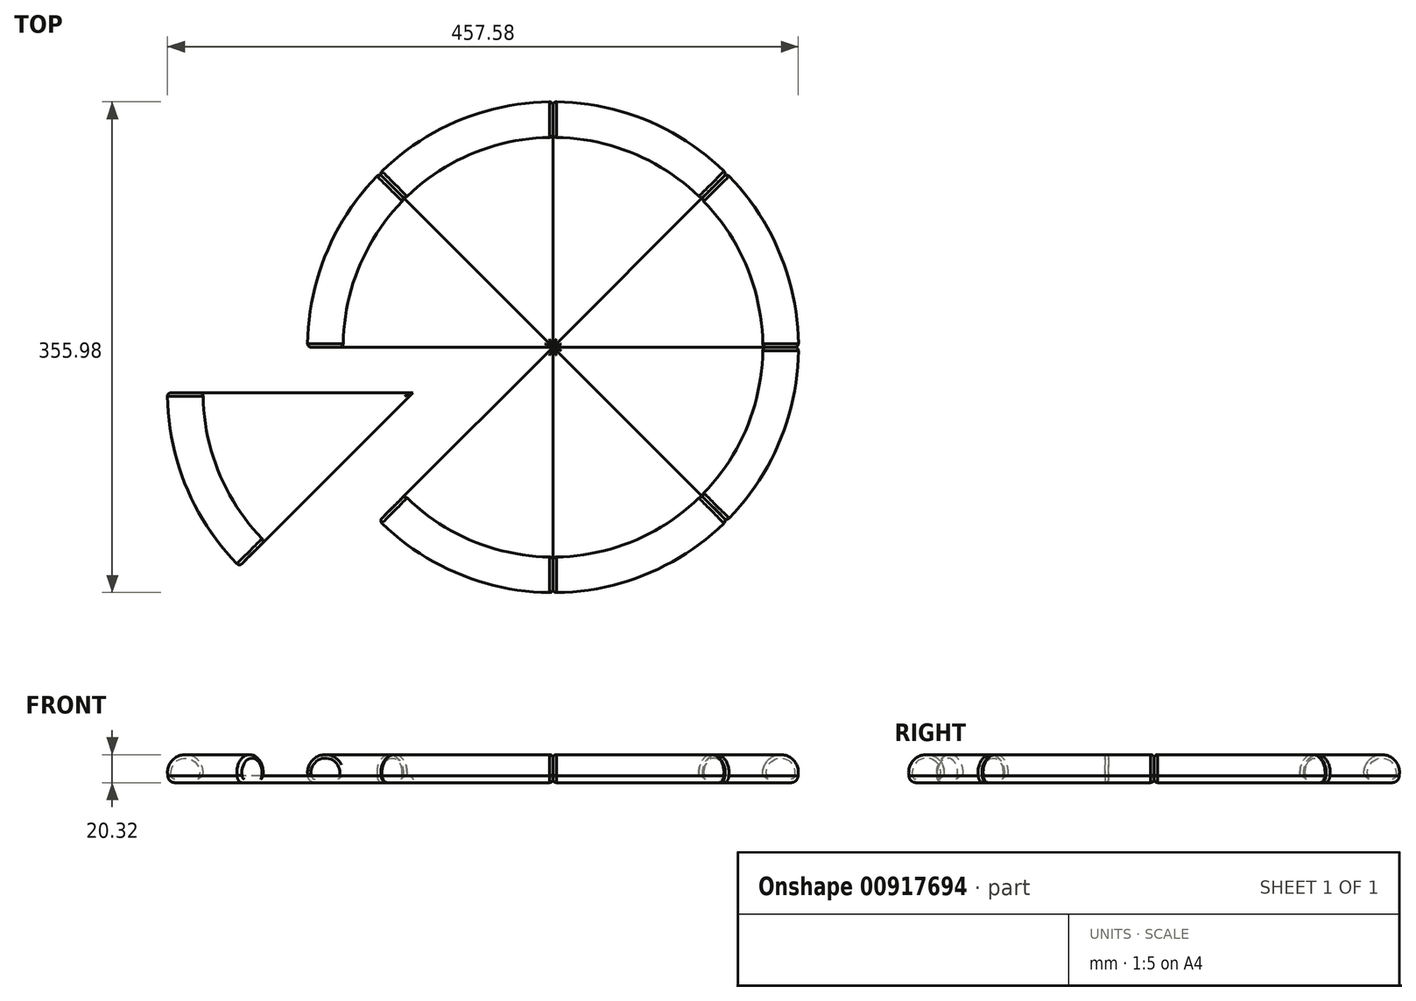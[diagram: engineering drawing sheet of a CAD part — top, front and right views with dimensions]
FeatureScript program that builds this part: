
annotation { "Feature Type Name" : "Feature", "Feature Type Description" : "" }
export const myFeature = defineFeature(function(context is Context, id is Id, definition is map)
    precondition{}
    {
        {
            var Q0;
            Q0=qCreatedBy(makeId("Top.planeOp"),FACE);
            var sketch = newSketch(context, id + "F0", { "sketchPlane" : qUnion([Q0])});
            skCircle(sketch, "E0", {"center": v(0, 0) * mm, "radius": 177.8 * mm});
            skSolve(sketch);
        }
        {
            var Q0;
            Q0=qCreatedBy(makeId("Front.planeOp"),FACE);
            var sketch = newSketch(context, id + "F1", { "sketchPlane" : qUnion([Q0])});
            skLineSegment(sketch, "E1.0", {"start": v(-177.8, 0) * mm, "end": v(177.8, 0) * mm});
            skArc(sketch, "E2", {"start": v(-152.4, 0) * mm, "mid": v(-165.1, 15.24) * mm, "end": v(-177.8, 0) * mm});
            skSolve(sketch);
        }
        {
            var Q0;
            {var subQ0=sQuery(id+"F1.wireOp",EDGE,"E2");Q0=makeQuery(id+"F1.imprint","IMPRINT",FACE,{"disambiguationData":[TD([[makeQuery(id+"F1.imprint","IMPRINT",EDGE,{"derivedFrom":subQ0}),1.0]])]});}
            var Q1;
            Q1=sQuery(id+"F0.wireOp",EDGE,"E0");
            revolve(context, id + "F2", {"surfaceOperationType" : NewSurfaceOperationType.NEW, "entities" : qUnion([Q0]), "axis" : qUnion([Q1]), "revolveType" : RevolveType.FULL});
        }
        {
            var Q0;
            Q0 = qSketchRegion(id + "F0", true);
            extrude(context, id + "F3", {"entities" : qUnion([Q0]), "operationType" : NewBodyOperationType.ADD, "oppositeDirection" : true, "depth" : 5.08 * mm, "offsetDistance" : 25.4 * mm});
        }
        {
            var Q0;
            Q0=makeQuery(id+"F3.opExtrude","CAP_EDGE",EDGE,{"disambiguationData":[OSD([sQuery(id+"F0.wireOp",EDGE,"E0")])],"isStart":false});
            fillet(context, id + "F4", {"entities" : qUnion([Q0]), "radius" : 5.08 * mm, "tangentPropagation" : true, "allowEdgeOverflow" : false});
        }
        {
            var Q0;
            Q0=qCreatedBy(makeId("Front.planeOp"),FACE);
            var sketch = newSketch(context, id + "F5", { "sketchPlane" : qUnion([Q0])});
            skLineSegment(sketch, "E3.right", {"start": v(-196.44, -103.09) * mm, "end": v(-196.44, 103.09) * mm});
            skPoint(sketch, "E3.middle", {"position": v(0, 0) * mm});
            skLineSegment(sketch, "E4", {"start": v(0, 0) * mm, "end": v(0, 103.09) * mm});
            skLineSegment(sketch, "E5", {"start": v(0, 0) * mm, "end": v(0, -103.09) * mm});
            skLineSegment(sketch, "E6", {"start": v(0, 103.09) * mm, "end": v(-196.44, 103.09) * mm});
            skLineSegment(sketch, "E7", {"start": v(0, -103.09) * mm, "end": v(-196.44, -103.09) * mm});
            skPoint(sketch, "E3.left.end.orphan", {"position": v(196.44, 103.09) * mm});
            skPoint(sketch, "E3.bottom.start.orphan", {"position": v(196.44, -103.09) * mm});
            skSolve(sketch);
        }
        {
            var Q0;
            Q0=makeQuery(id+"F5.imprint","IMPRINT",FACE,{"disambiguationData":[TD([[makeQuery(id+"F5.imprint","IMPRINT",EDGE,{"derivedFrom":sQuery(id+"F5.wireOp",EDGE,"E3.right")}),-1.0]])]});
            var Q1;
            Q1=sQuery(id+"F5.wireOp",EDGE,"E4");
            revolve(context, id + "F6", {"operationType" : NewBodyOperationType.REMOVE, "surfaceOperationType" : NewSurfaceOperationType.NEW, "entities" : qUnion([Q0]), "axis" : qUnion([Q1]), "revolveType" : RevolveType.ONE_DIRECTION, "oppositeDirection" : true, "angle" : 315 * degree});
        }
        {
            var Q0;
            Q0=makeQuery(id+"F6.boolean.opBoolean","INTERSECT",EDGE,{"derivedFrom":[makeQuery(id+"F3.opExtrude","CAP_FACE",FACE,{"disambiguationData":[OSD([sQuery(id+"F0.wireOp",EDGE,"E0")])],"isStart":true}),makeQuery(id+"F6.opRevolve","CAP_FACE",FACE,{"disambiguationData":[OSD([sQuery(id+"F5.wireOp",EDGE,"E3.right"),sQuery(id+"F5.wireOp",EDGE,"E4"),sQuery(id+"F5.wireOp",EDGE,"E5"),sQuery(id+"F5.wireOp",EDGE,"E6"),sQuery(id+"F5.wireOp",EDGE,"E7")])],"isStart":false})]});
            var Q1;
            Q1=makeQuery(id+"F6.boolean.opBoolean","INTERSECT",EDGE,{"derivedFrom":[makeQuery(id+"F3.opExtrude","CAP_FACE",FACE,{"disambiguationData":[OSD([sQuery(id+"F0.wireOp",EDGE,"E0")])],"isStart":true}),makeQuery(id+"F6.opRevolve","CAP_FACE",FACE,{"disambiguationData":[OSD([sQuery(id+"F5.wireOp",EDGE,"E3.right"),sQuery(id+"F5.wireOp",EDGE,"E4"),sQuery(id+"F5.wireOp",EDGE,"E5"),sQuery(id+"F5.wireOp",EDGE,"E6"),sQuery(id+"F5.wireOp",EDGE,"E7")])],"isStart":true})]});
            var Q2;
            Q2=makeQuery(id+"F6.boolean.opBoolean","INTERSECT",EDGE,{"derivedFrom":[makeQuery(id+"F2.opRevolve","SWEPT_FACE",FACE,{"disambiguationData":[OSD([sQuery(id+"F1.wireOp",EDGE,"E2")])]}),makeQuery(id+"F6.opRevolve","CAP_FACE",FACE,{"disambiguationData":[OSD([sQuery(id+"F5.wireOp",EDGE,"E3.right"),sQuery(id+"F5.wireOp",EDGE,"E4"),sQuery(id+"F5.wireOp",EDGE,"E5"),sQuery(id+"F5.wireOp",EDGE,"E6"),sQuery(id+"F5.wireOp",EDGE,"E7")])],"isStart":true})]});
            var Q3;
            Q3=makeQuery(id+"F6.boolean.opBoolean","INTERSECT",EDGE,{"derivedFrom":[makeQuery(id+"F4.opFillet","BLEND_FACE",FACE,{"disambiguationData":[OSD([sQuery(id+"F0.wireOp",EDGE,"E0")])]}),makeQuery(id+"F6.opRevolve","CAP_FACE",FACE,{"disambiguationData":[OSD([sQuery(id+"F5.wireOp",EDGE,"E3.right"),sQuery(id+"F5.wireOp",EDGE,"E4"),sQuery(id+"F5.wireOp",EDGE,"E5"),sQuery(id+"F5.wireOp",EDGE,"E6"),sQuery(id+"F5.wireOp",EDGE,"E7")])],"isStart":true})]});
            var Q4;
            Q4=makeQuery(id+"F6.boolean.opBoolean","INTERSECT",EDGE,{"derivedFrom":[makeQuery(id+"F2.opRevolve","SWEPT_FACE",FACE,{"disambiguationData":[OSD([sQuery(id+"F1.wireOp",EDGE,"E2")])]}),makeQuery(id+"F6.opRevolve","CAP_FACE",FACE,{"disambiguationData":[OSD([sQuery(id+"F5.wireOp",EDGE,"E3.right"),sQuery(id+"F5.wireOp",EDGE,"E4"),sQuery(id+"F5.wireOp",EDGE,"E5"),sQuery(id+"F5.wireOp",EDGE,"E6"),sQuery(id+"F5.wireOp",EDGE,"E7")])],"isStart":false})]});
            var Q5;
            Q5=makeQuery(id+"F6.boolean.opBoolean","INTERSECT",EDGE,{"derivedFrom":[makeQuery(id+"F4.opFillet","BLEND_FACE",FACE,{"disambiguationData":[OSD([sQuery(id+"F0.wireOp",EDGE,"E0")])]}),makeQuery(id+"F6.opRevolve","CAP_FACE",FACE,{"disambiguationData":[OSD([sQuery(id+"F5.wireOp",EDGE,"E3.right"),sQuery(id+"F5.wireOp",EDGE,"E4"),sQuery(id+"F5.wireOp",EDGE,"E5"),sQuery(id+"F5.wireOp",EDGE,"E6"),sQuery(id+"F5.wireOp",EDGE,"E7")])],"isStart":false})]});
            fillet(context, id + "F7", {"entities" : qUnion([Q0, Q1, Q2, Q3, Q4, Q5]), "radius" : 2.54 * mm, "tangentPropagation" : true, "allowEdgeOverflow" : false});
        }
        {
            var Q0;
            Q0=qCreatedBy(makeId("Front.planeOp"),FACE);
            var sketch = newSketch(context, id + "F8", { "sketchPlane" : qUnion([Q0])});
            skLineSegment(sketch, "E8", {"start": v(0, 0) * mm, "end": v(0, 70.28) * mm});
            skSolve(sketch);
        }
        {
            var Q0;
            Q0=makeQuery(id+"F2.opRevolve","SWEPT_BODY",BODY,{"disambiguationData":[OSD([sQuery(id+"F1.wireOp",EDGE,"E1.0"),sQuery(id+"F1.wireOp",EDGE,"E2")])]});
            var Q1;
            Q1=sQuery(id+"F8.wireOp",EDGE,"E8");
            circularPattern(context, id + "F9", {"entities" : qUnion([Q0]), "axis" : qUnion([Q1]), "angle" : 360 * degree, "instanceCount" : 8, "equalSpace" : true});
        }
        {
            var Q0;
            Q0=makeQuery(id+"F2.opRevolve","SWEPT_BODY",BODY,{"disambiguationData":[OSD([sQuery(id+"F1.wireOp",EDGE,"E1.0"),sQuery(id+"F1.wireOp",EDGE,"E2")])]});
            transform(context, id + "F10", {"entities" : qUnion([Q0]), "transformType" : TransformType.TRANSLATION_3D, "dx" : -101.6 * mm, "dy" : -33.02 * mm, "dz" : 0 * mm, "makeCopy" : false});
        }
    });
